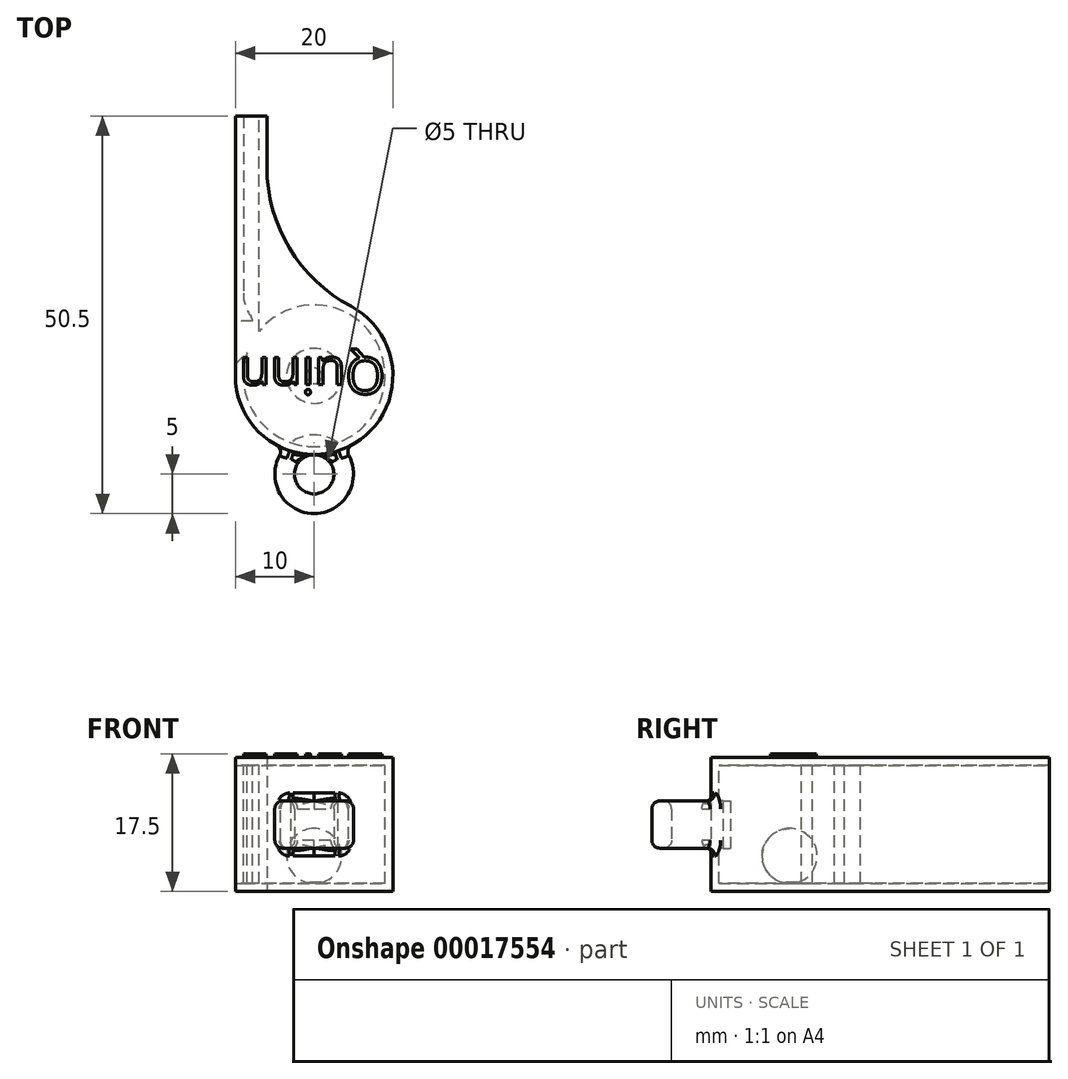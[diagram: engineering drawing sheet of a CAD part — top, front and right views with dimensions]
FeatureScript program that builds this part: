
annotation { "Feature Type Name" : "Feature", "Feature Type Description" : "" }
export const myFeature = defineFeature(function(context is Context, id is Id, definition is map)
    precondition{}
    {
        {
            var Q0;
            Q0=qCreatedBy(makeId("Top.planeOp"),FACE);
            var sketch = newSketch(context, id + "F0", { "sketchPlane" : qUnion([Q0])});
            skArc(sketch, "E0.0.4", {"start": v(-10, 0) * mm, "mid": v(5.16, -8.56) * mm, "end": v(4.67, 8.84) * mm});
            skLineSegment(sketch, "E0.0.3", {"start": v(-10, 33) * mm, "end": v(-10, 0) * mm});
            skLineSegment(sketch, "E0.0.2", {"start": v(-6, 33) * mm, "end": v(-10, 33) * mm});
            skLineSegment(sketch, "E0.0.1", {"start": v(-6, 26.53) * mm, "end": v(-6, 33) * mm});
            skArc(sketch, "E0.0.0", {"start": v(4.67, 8.84) * mm, "mid": v(-3.13, 16.2) * mm, "end": v(-6, 26.53) * mm});
            skSolve(sketch);
        }
        {
            var Q0;
            Q0=makeQuery(id+"F0.imprint","IMPRINT",FACE,{"disambiguationData":[TD([[makeQuery(id+"F0.imprint","IMPRINT",EDGE,{"derivedFrom":sQuery(id+"F0.wireOp",EDGE,"E0.0.4")}),1.0]])]});
            extrude(context, id + "F1", {"entities" : qUnion([Q0]), "endBound" : BoundingType.SYMMETRIC, "depth" : 17 * mm});
        }
        {
            var Q0;
            Q0=qCreatedBy(makeId("Top.planeOp"),FACE);
            var sketch = newSketch(context, id + "F2", { "sketchPlane" : qUnion([Q0])});
            skLineSegment(sketch, "E1.0", {"start": v(-9, 33) * mm, "end": v(-9, 10.5) * mm});
            skLineSegment(sketch, "E2.0", {"start": v(-7, 5.66) * mm, "end": v(-7, 33) * mm});
            skArc(sketch, "E3.0", {"start": v(-8.53, 2.87) * mm, "mid": v(7.89, -4.33) * mm, "end": v(-7, 5.66) * mm});
            skLineSegment(sketch, "E4.0", {"start": v(-10, 1.48) * mm, "end": v(-8.58, 2.9) * mm});
            skArc(sketch, "E5.0", {"start": v(-8.03, 7.54) * mm, "mid": v(-8.75, 8.94) * mm, "end": v(-9, 10.5) * mm});
            skArc(sketch, "E6.0", {"start": v(-7.8, 6.95) * mm, "mid": v(-7.87, 7.26) * mm, "end": v(-8.03, 7.54) * mm});
            skLineSegment(sketch, "E7.0", {"start": v(-7.8, 6.95) * mm, "end": v(-10, 6.95) * mm});
            skLineSegment(sketch, "E8", {"start": v(-7, 33) * mm, "end": v(-9, 33) * mm});
            skLineSegment(sketch, "E9", {"start": v(-10, 6.95) * mm, "end": v(-10, 1.48) * mm});
            skPoint(sketch, "E10.visualSharp", {"position": v(-8.49, 3) * mm});
            skArc(sketch, "E10.filletArc", {"start": v(-8.53, 2.87) * mm, "mid": v(-8.54, 2.9) * mm, "end": v(-8.58, 2.9) * mm});
            skSolve(sketch);
        }
        {
            var Q0;
            Q0=makeQuery(id+"F2.imprint","IMPRINT",FACE,{"disambiguationData":[TD([[makeQuery(id+"F2.imprint","IMPRINT",EDGE,{"derivedFrom":sQuery(id+"F2.wireOp",EDGE,"E1.0")}),1.0]])]});
            extrude(context, id + "F3", {"entities" : qUnion([Q0]), "operationType" : NewBodyOperationType.REMOVE, "endBound" : BoundingType.SYMMETRIC, "oppositeDirection" : true, "depth" : 15 * mm});
        }
        {
            var Q0;
            Q0=qCreatedBy(makeId("Right.planeOp"),FACE);
            var sketch = newSketch(context, id + "F4", { "sketchPlane" : qUnion([Q0])});
            skArc(sketch, "E11", {"start": v(0, -7.5) * mm, "mid": v(3.5, -4) * mm, "end": v(0, -0.5) * mm});
            skLineSegment(sketch, "E12.0", {"start": v(-9, -7.5) * mm, "end": v(9, -7.5) * mm, "construction": true});
            skLineSegment(sketch, "E13", {"start": v(0, 3.94) * mm, "end": v(0, -16.8) * mm, "construction": true});
            skLineSegment(sketch, "E14", {"start": v(0, -7.5) * mm, "end": v(0, -0.5) * mm});
            skSolve(sketch);
        }
        {
            var Q0;
            Q0=makeQuery(id+"F4.imprint","IMPRINT",FACE,{"disambiguationData":[TD([[makeQuery(id+"F4.imprint","IMPRINT",EDGE,{"derivedFrom":sQuery(id+"F4.wireOp",EDGE,"E11")}),1.0]])]});
            var Q1;
            Q1=sQuery(id+"F4.wireOp",EDGE,"E11");
            var Q2;
            Q2=sQuery(id+"F4.wireOp",EDGE,"E13");
            revolve(context, id + "F5", {"entities" : qUnion([Q0]), "surfaceEntities" : qUnion([Q1]), "axis" : qUnion([Q2]), "revolveType" : RevolveType.FULL});
        }
        {
            var Q0;
            Q0=qCreatedBy(makeId("Top.planeOp"),FACE);
            var sketch = newSketch(context, id + "F6", { "sketchPlane" : qUnion([Q0])});
            skArc(sketch, "E15", {"start": v(-3.8, -9.25) * mm, "mid": v(0, -17.5) * mm, "end": v(3.8, -9.25) * mm});
            skCircle(sketch, "E16", {"center": v(0, -12.5) * mm, "radius": 2.5 * mm});
            skPoint(sketch, "E17.orphan", {"position": v(-10, 0) * mm});
            skPoint(sketch, "E18.orphan", {"position": v(4.67, 8.84) * mm});
            skArc(sketch, "E19", {"start": v(-3.8, -9.25) * mm, "mid": v(0, -7.5) * mm, "end": v(3.8, -9.25) * mm});
            skSolve(sketch);
        }
        {
            var Q0;
            {var subQ1=sQuery(id+"F6.wireOp",EDGE,"E15");Q0=makeQuery(id+"F6.imprint","IMPRINT",FACE,{"disambiguationData":[TD([[makeQuery(id+"F6.imprint","IMPRINT",EDGE,{"derivedFrom":subQ1}),1.0]])]});}
            extrude(context, id + "F7", {"entities" : qUnion([Q0]), "operationType" : NewBodyOperationType.ADD, "endBound" : BoundingType.SYMMETRIC, "depth" : 6 * mm});
        }
        {
            var Q0;
            {var subQ0=sQuery(id+"F6.wireOp",EDGE,"E15");var subQ1=sQuery(id+"F6.wireOp",EDGE,"E19");Q0=makeQuery(id+"F7.boolean.opBoolean","SPLIT",FACE,{"disambiguationData":[TD([makeQuery(id+"F1.opExtrude","SWEPT_FACE",FACE,{"disambiguationData":[OSD([sQuery(id+"F0.wireOp",EDGE,"E0.0.4")])]})])],"derivedFrom":makeQuery(id+"F7.opExtrude","SWEPT_FACE",FACE,{"disambiguationData":[OSD([subQ0,subQ1])]})});}
            var Q1;
            {var subQ0=sQuery(id+"F6.wireOp",EDGE,"E15");var subQ1=sQuery(id+"F6.wireOp",EDGE,"E16");var subQ2=sQuery(id+"F6.wireOp",EDGE,"E19");Q1=makeQuery(id+"F7.boolean.opBoolean","SPLIT",FACE,{"disambiguationData":[TD([makeQuery(id+"F1.opExtrude","SWEPT_FACE",FACE,{"disambiguationData":[OSD([sQuery(id+"F0.wireOp",EDGE,"E0.0.4")])]})])],"derivedFrom":makeQuery(id+"F7.opExtrude","CAP_FACE",FACE,{"disambiguationData":[OSD([subQ0,subQ1,subQ2])],"isStart":false})});}
            var Q2;
            {var subQ0=sQuery(id+"F6.wireOp",EDGE,"E15");var subQ1=sQuery(id+"F6.wireOp",EDGE,"E16");var subQ2=sQuery(id+"F6.wireOp",EDGE,"E19");Q2=makeQuery(id+"F7.boolean.opBoolean","SPLIT",FACE,{"disambiguationData":[TD([makeQuery(id+"F1.opExtrude","SWEPT_FACE",FACE,{"disambiguationData":[OSD([sQuery(id+"F0.wireOp",EDGE,"E0.0.4")])]})])],"derivedFrom":makeQuery(id+"F7.opExtrude","CAP_FACE",FACE,{"disambiguationData":[OSD([subQ0,subQ1,subQ2])],"isStart":true})});}
            var Q3;
            Q3=makeQuery(id+"F3.boolean.opBoolean","COPY",EDGE,{"derivedFrom":makeQuery(id+"F3.opExtrude","CAP_EDGE",EDGE,{"disambiguationData":[OSD([sQuery(id+"F2.wireOp",EDGE,"E8")])],"isStart":true})});
            var Q4;
            Q4=makeQuery(id+"F3.boolean.opBoolean","COPY",EDGE,{"derivedFrom":makeQuery(id+"F3.opExtrude","SWEPT_EDGE",EDGE,{"disambiguationData":[OSD([sQuery(id+"F2.wireOp",EDGE,"E1.0"),sQuery(id+"F2.wireOp",EDGE,"E8")])]})});
            var Q5;
            Q5=makeQuery(id+"F3.boolean.opBoolean","COPY",EDGE,{"derivedFrom":makeQuery(id+"F3.opExtrude","SWEPT_EDGE",EDGE,{"disambiguationData":[OSD([sQuery(id+"F2.wireOp",EDGE,"E2.0"),sQuery(id+"F2.wireOp",EDGE,"E8")])]})});
            var Q6;
            Q6=makeQuery(id+"F3.boolean.opBoolean","COPY",EDGE,{"derivedFrom":makeQuery(id+"F3.opExtrude","CAP_EDGE",EDGE,{"disambiguationData":[OSD([sQuery(id+"F2.wireOp",EDGE,"E8")])],"isStart":false})});
            fillet(context, id + "F8", {"entities" : qUnion([Q0, Q1, Q2, Q3, Q4, Q5, Q6]), "radius" : 1 * mm, "tangentPropagation" : true, "allowEdgeOverflow" : false});
        }
        {
            var Q0;
            Q0=makeQuery(id+"F1.opExtrude","CAP_FACE",FACE,{"disambiguationData":[OSD([sQuery(id+"F0.wireOp",EDGE,"E0.0.4"),sQuery(id+"F0.wireOp",EDGE,"E0.0.3"),sQuery(id+"F0.wireOp",EDGE,"E0.0.2"),sQuery(id+"F0.wireOp",EDGE,"E0.0.1"),sQuery(id+"F0.wireOp",EDGE,"E0.0.0")])],"isStart":false});
            var sketch = newSketch(context, id + "F9", { "sketchPlane" : qUnion([Q0])});
            skText(sketch, "E20", { "text": "Quinn", "fontName": "OpenSans-Regular.ttf"});
            const initialGuessF9  = {"E20": [0.009, 0.00232, -1, 0, 0.00464]};
            skSetInitialGuess(sketch, initialGuessF9);
            skSolve(sketch);
        }
        {
            var Q0;
            Q0 = qSketchRegion(id + "F9", true);
            extrude(context, id + "F10", {"entities" : qUnion([Q0]), "operationType" : NewBodyOperationType.ADD, "depth" : 0.5 * mm});
        }
        {
            var Q0;
            Q0=makeQuery(id+"F3.boolean.opBoolean","COPY",FACE,{"derivedFrom":makeQuery(id+"F3.opExtrude","CAP_FACE",FACE,{"disambiguationData":[OSD([sQuery(id+"F2.wireOp",EDGE,"E1.0"),sQuery(id+"F2.wireOp",EDGE,"E2.0"),sQuery(id+"F2.wireOp",EDGE,"E3.0"),sQuery(id+"F2.wireOp",EDGE,"E4.0"),sQuery(id+"F2.wireOp",EDGE,"E5.0"),sQuery(id+"F2.wireOp",EDGE,"E6.0"),sQuery(id+"F2.wireOp",EDGE,"E7.0"),sQuery(id+"F2.wireOp",EDGE,"E8"),sQuery(id+"F2.wireOp",EDGE,"E9"),sQuery(id+"F2.wireOp",EDGE,"E10.filletArc")])],"isStart":false})});
            var sketch = newSketch(context, id + "F11", { "sketchPlane" : qUnion([Q0])});
            skCircle(sketch, "E21", {"center": v(0, 0) * mm, "radius": 1 * mm});
            skSolve(sketch);
        }
        {
            var Q0;
            Q0 = qSketchRegion(id + "F11", true);
            extrude(context, id + "F12", {"entities" : qUnion([Q0]), "operationType" : NewBodyOperationType.ADD, "depth" : 2 * mm});
        }
    });
